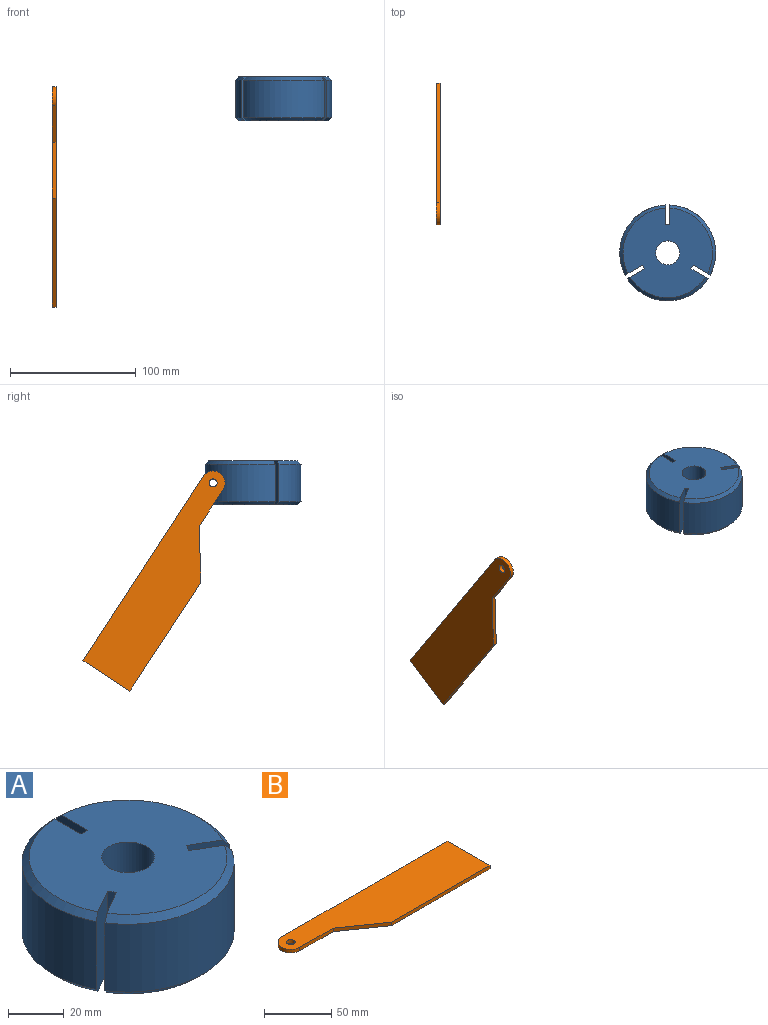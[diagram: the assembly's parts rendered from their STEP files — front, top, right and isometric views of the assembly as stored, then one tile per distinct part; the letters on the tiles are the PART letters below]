
ASSEMBLY  parts=2 mates=2
PART A: 23 faces, bbox 76.2x76.2x34.9 mm
  f0: cylinder r=38.1mm len=55.67mm, axis (0,0,-1), area 2223.8mm2, adj f5,f8,f14,f19,f22
  f1: cylinder r=38.1mm len=55.67mm, axis (0,0,-1), area 2225.1mm2, adj f6,f9,f16,f20,f21
  f2: cylinder r=38.1mm len=64.28mm, axis (0,0,-1), area 2282.9mm2, adj f7,f10,f13,f17
  f3: plane 71.12x71.08mm, normal (0,0,1), area 3555.6mm2, adj f8,f9,f10,f11,f12,f13,f14,f15
  f4: plane 71.12x71.08mm, normal (0,0,-1), area 3555.6mm2, adj f5,f6,f7,f11,f12,f13,f14,f15
  f5: cone r=38.1mm half-angle=45deg, axis (0,0,1), area 265.2mm2, adj f0,f4,f14,f19
  f6: cone r=38.1mm half-angle=45deg, axis (0,0,1), area 265.2mm2, adj f1,f4,f16,f20
  f7: cone r=38.1mm half-angle=45deg, axis (0,0,1), area 265.2mm2, adj f2,f4,f13,f17
  f8: cone r=35.56mm half-angle=45deg, axis (0,0,-1), area 265.2mm2, adj f0,f3,f14,f19
  f9: cone r=35.56mm half-angle=45deg, axis (0,0,-1), area 265.2mm2, adj f1,f3,f16,f20
  f10: cone r=35.56mm half-angle=45deg, axis (0,0,-1), area 265.2mm2, adj f2,f3,f13,f17
  f11: cylinder r=9.53mm len=34.93mm, axis (0,0,-1), area 2090.2mm2, adj f3,f4
  f12: plane 34.93x2.86mm, normal (0.87,-0.5,0), area 115.3mm2, adj f3,f4,f13,f14
  f13: plane 34.93x13.72mm, normal (0.5,0.87,0), area 546.7mm2, adj f2,f3,f4,f7,f10,f12
  f14: plane 34.93x13.72mm, normal (-0.5,-0.87,0), area 546.7mm2, adj f0,f3,f4,f5,f8,f12
  f15: plane 34.93x2.86mm, normal (-0.87,-0.5,0), area 115.3mm2, adj f3,f4,f16,f17
  f16: plane 34.93x13.72mm, normal (0.5,-0.87,0), area 546.7mm2, adj f1,f3,f4,f6,f9,f15
  f17: plane 34.93x13.72mm, normal (-0.5,0.87,0), area 546.7mm2, adj f2,f3,f4,f7,f10,f15
  f18: plane 34.93x3.3mm, normal (0,1,0), area 115.3mm2, adj f3,f4,f19,f20
  f19: plane 34.93x15.84mm, normal (-1,0,0), area 515.1mm2, adj f0,f3,f4,f5,f8,f18,f22
  f20: plane 34.93x15.84mm, normal (1,0,0), area 515.1mm2, adj f1,f3,f4,f6,f9,f18,f21
  f21: cylinder r=3.17mm len=23.55mm, axis (1,0,0), area 378.9mm2, adj f1,f20
  f22: cylinder r=3.17mm len=23.55mm, axis (1,0,0), area 378.9mm2, adj f0,f19
PART B: 9 faces, bbox 184x44.5x3.2 mm
  f0: plane 44.45x3.18mm, normal (1,0,0), area 141.1mm2, adj f1,f4,f6,f7
  f1: plane 174.43x3.18mm, normal (0,1,0), area 553.8mm2, adj f0,f6,f7,f8
  f2: plane 34.93x3.18mm, normal (0,-1,0), area 110.9mm2, adj f3,f6,f7,f8
  f3: plane 36.28x25.4mm, normal (-0.57,-0.82,0), area 140.6mm2, adj f2,f4,f6,f7
  f4: plane 103.23x3.18mm, normal (0,-1,0), area 327.8mm2, adj f0,f3,f6,f7
  f5: cylinder r=3.17mm len=6.35mm, axis (0,0,-1), area 63.3mm2, adj f6,f7
  f6: plane 183.95x44.45mm, normal (0,0,1), area 6516.5mm2, adj f0,f1,f2,f3,f4,f5,f8
  f7: plane 183.95x44.45mm, normal (0,0,-1), area 6516.5mm2, adj f0,f1,f2,f3,f4,f5,f8
  f8: cylinder r=9.53mm len=19.05mm, axis (0,0,-1), area 95mm2, adj f1,f2,f6,f7
PLACE A t=(-11.09,5,-0.38)mm fixed
PLACE B rot(axis=(0.27,0.92,0.27),94.7deg) t=(-194.84,39.52,30.27)mm
MATE cylindrical B.f5 <-> A.f21  axis (-1,0,0) through (-194.84,36.75,17.09)mm
MATE parallel A.f21 <-> B.f5  axis (1,0,0) through (-9.44,36.75,17.09)mm
